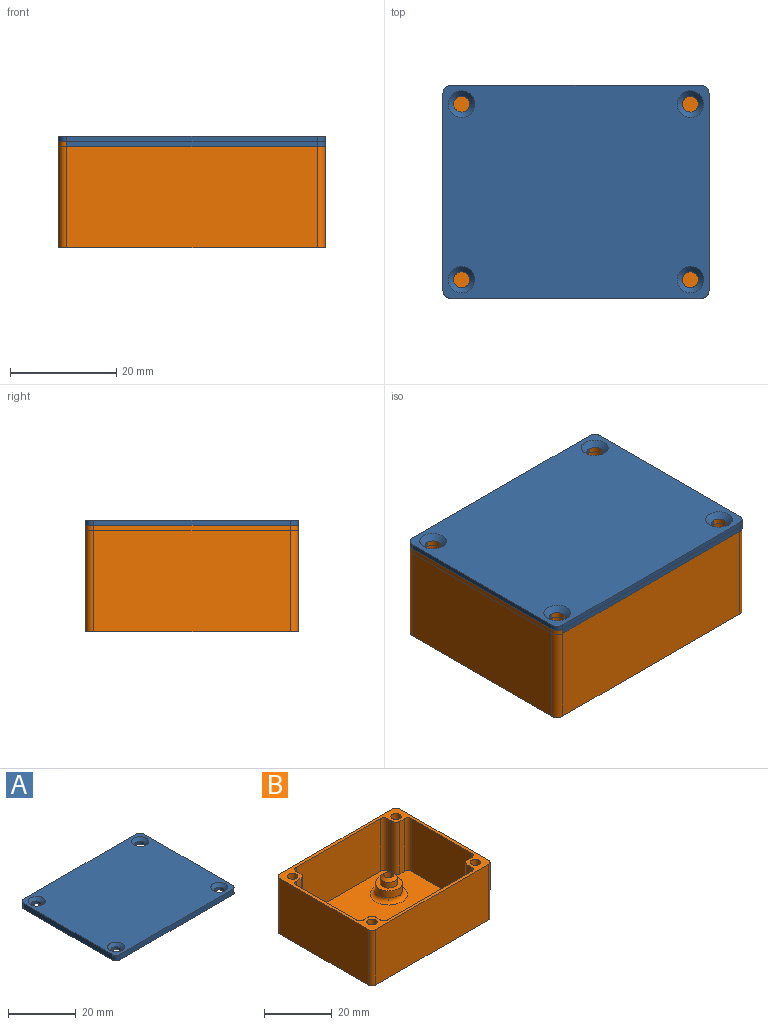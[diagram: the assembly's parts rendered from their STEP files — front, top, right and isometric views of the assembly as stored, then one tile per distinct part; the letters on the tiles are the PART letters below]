
ASSEMBLY  parts=2 mates=1
PART A: 18 faces, bbox 50x40x2 mm
  f0: plane 47x2mm, normal (0,1,0), area 94mm2, adj f4,f5,f14,f17
  f1: plane 37x2mm, normal (-1,0,0), area 74mm2, adj f4,f5,f14,f15
  f2: plane 47x2mm, normal (0,-1,0), area 94mm2, adj f4,f5,f15,f16
  f3: plane 37x2mm, normal (1,0,0), area 74mm2, adj f4,f5,f16,f17
  f4: plane 50x40mm, normal (0,0,1), area 1919.5mm2, adj f0,f1,f2,f3,f10,f11,f12,f13
  f5: plane 50x40mm, normal (0,0,-1), area 1969.8mm2, adj f0,f1,f2,f3,f6,f7,f8,f9
  f6: cylinder r=1.5mm len=3mm, axis (0,0,1), area 9.4mm2, adj f5,f13
  f7: cylinder r=1.5mm len=3mm, axis (0,0,1), area 9.4mm2, adj f5,f12
  f8: cylinder r=1.5mm len=3mm, axis (0,0,1), area 9.4mm2, adj f5,f11
  f9: cylinder r=1.5mm len=3mm, axis (0,0,1), area 9.4mm2, adj f5,f10
  f10: cone r=1.5mm half-angle=45deg, axis (0,0,1), area 17.8mm2, adj f4,f9
  f11: cone r=1.5mm half-angle=45deg, axis (0,0,1), area 17.8mm2, adj f4,f8
  f12: cone r=1.5mm half-angle=45deg, axis (0,0,1), area 17.8mm2, adj f4,f7
  f13: cone r=1.5mm half-angle=45deg, axis (0,0,1), area 17.8mm2, adj f4,f6
  f14: cylinder r=1.5mm len=2mm, axis (0,0,1), area 4.7mm2, adj f0,f1,f4,f5
  f15: cylinder r=1.5mm len=2mm, axis (0,0,-1), area 4.7mm2, adj f1,f2,f4,f5
  f16: cylinder r=1.5mm len=2mm, axis (0,0,1), area 4.7mm2, adj f2,f3,f4,f5
  f17: cylinder r=1.5mm len=2mm, axis (0,0,-1), area 4.7mm2, adj f0,f3,f4,f5
PART B: 95 faces, bbox 50x40x20 mm
  f0: cylinder r=1.5mm len=6mm, axis (0,0,-1), area 56.5mm2, adj f90,f94
  f1: cylinder r=1.5mm len=6mm, axis (0,0,-1), area 56.5mm2, adj f83,f91
  f2: cylinder r=1.5mm len=6mm, axis (0,0,-1), area 56.5mm2, adj f76,f93
  f3: cylinder r=1.5mm len=6mm, axis (0,0,-1), area 56.5mm2, adj f69,f92
  f4: plane 48x38mm, normal (0,0,1), area 1341.9mm2, adj f5,f6,f7,f8,f15,f16,f17,f18
  f5: plane 35x19mm, normal (0,1,0), area 665mm2, adj f4,f9,f48,f50
  f6: plane 25x19mm, normal (-1,0,0), area 475mm2, adj f4,f9,f52,f53
  f7: plane 35x19mm, normal (0,-1,0), area 665mm2, adj f4,f9,f54,f56
  f8: plane 25x19mm, normal (1,0,0), area 475mm2, adj f4,f9,f49,f58
  f9: plane 50x40mm, normal (0,0,1), area 247.7mm2, adj f5,f6,f7,f8,f10,f11,f12,f13
  f10: plane 47x20mm, normal (0,-1,0), area 940mm2, adj f9,f14,f59,f62
  f11: plane 37x20mm, normal (1,0,0), area 740mm2, adj f9,f14,f59,f60
  f12: plane 47x20mm, normal (0,1,0), area 940mm2, adj f9,f14,f60,f61
  f13: plane 37x20mm, normal (-1,0,0), area 740mm2, adj f9,f14,f61,f62
  f14: plane 50x40mm, normal (0,0,-1), area 1831.8mm2, adj f10,f11,f12,f13,f59,f60,f61,f62
  f15: plane 19x2mm, normal (0,-1,0), area 38mm2, adj f4,f9,f57,f58
  f16: plane 19x2mm, normal (1,0,0), area 38mm2, adj f4,f9,f56,f57
  f17: plane 19x2mm, normal (0,-1,0), area 38mm2, adj f4,f9,f53,f55
  f18: plane 19x2mm, normal (-1,0,0), area 38mm2, adj f4,f9,f54,f55
  f19: plane 19x2mm, normal (0,1,0), area 38mm2, adj f4,f9,f47,f49
  f20: plane 19x2mm, normal (1,0,0), area 38mm2, adj f4,f9,f47,f48
  f21: plane 19x2mm, normal (0,1,0), area 38mm2, adj f4,f9,f51,f52
  f22: plane 19x2mm, normal (-1,0,0), area 38mm2, adj f4,f9,f50,f51
  f23: cylinder r=1.5mm len=10mm, axis (0,0,1), area 94.2mm2, adj f9,f24
  f24: plane 3x3mm, normal (0,0,1), area 7.1mm2, adj f23
  f25: cylinder r=1.5mm len=10mm, axis (0,0,1), area 94.2mm2, adj f9,f26
  f26: plane 3x3mm, normal (0,0,1), area 7.1mm2, adj f25
  f27: cylinder r=1.5mm len=10mm, axis (0,0,1), area 94.2mm2, adj f9,f28
  f28: plane 3x3mm, normal (0,0,1), area 7.1mm2, adj f27
  f29: cylinder r=1.5mm len=10mm, axis (0,0,1), area 94.2mm2, adj f9,f30
  f30: plane 3x3mm, normal (0,0,1), area 7.1mm2, adj f29
  f31: cylinder r=2.5mm len=5mm, axis (0,0,-1), area 31.4mm2, adj f42,f94
  f32: cylinder r=2.5mm len=5mm, axis (0,0,-1), area 31.4mm2, adj f40,f91
  f33: cylinder r=2.5mm len=5mm, axis (0,0,-1), area 31.4mm2, adj f38,f93
  f34: cylinder r=2.5mm len=5mm, axis (0,0,-1), area 31.4mm2, adj f36,f92
  f35: cylinder r=4mm len=8mm, axis (0,0,-1), area 62.8mm2, adj f36,f46
  f36: plane 8x8mm, normal (0,0,1), area 30.6mm2, adj f34,f35
  f37: cylinder r=4mm len=8mm, axis (0,0,-1), area 62.8mm2, adj f38,f45
  f38: plane 8x8mm, normal (0,0,1), area 30.6mm2, adj f33,f37
  f39: cylinder r=4mm len=8mm, axis (0,0,-1), area 62.8mm2, adj f40,f44
  f40: plane 8x8mm, normal (0,0,1), area 30.6mm2, adj f32,f39
  f41: cylinder r=4mm len=8mm, axis (0,0,-1), area 62.8mm2, adj f42,f43
  f42: plane 8x8mm, normal (0,0,1), area 30.6mm2, adj f31,f41
  f43: torus R=5.5mm, axis (0,0,1), area 67.3mm2, adj f4,f41
  f44: torus R=5.5mm, axis (0,0,1), area 67.3mm2, adj f4,f39
  f45: torus R=5.5mm, axis (0,0,1), area 67.3mm2, adj f4,f37
  f46: torus R=5.5mm, axis (0,0,1), area 67.3mm2, adj f4,f35
  f47: cylinder r=1.5mm len=19mm, axis (0,0,1), area 44.8mm2, adj f4,f9,f19,f20
  f48: cylinder r=1.5mm len=19mm, axis (0,0,1), area 44.8mm2, adj f4,f5,f9,f20
  f49: cylinder r=1.5mm len=19mm, axis (0,0,-1), area 44.8mm2, adj f4,f8,f9,f19
  f50: cylinder r=1.5mm len=19mm, axis (0,0,-1), area 44.8mm2, adj f4,f5,f9,f22
  f51: cylinder r=1.5mm len=19mm, axis (0,0,1), area 44.8mm2, adj f4,f9,f21,f22
  f52: cylinder r=1.5mm len=19mm, axis (0,0,-1), area 44.8mm2, adj f4,f6,f9,f21
  f53: cylinder r=1.5mm len=19mm, axis (0,0,1), area 44.8mm2, adj f4,f6,f9,f17
  f54: cylinder r=1.5mm len=19mm, axis (0,0,-1), area 44.8mm2, adj f4,f7,f9,f18
  f55: cylinder r=1.5mm len=19mm, axis (0,0,1), area 44.8mm2, adj f4,f9,f17,f18
  f56: cylinder r=1.5mm len=19mm, axis (0,0,1), area 44.8mm2, adj f4,f7,f9,f16
  f57: cylinder r=1.5mm len=19mm, axis (0,0,1), area 44.8mm2, adj f4,f9,f15,f16
  f58: cylinder r=1.5mm len=19mm, axis (0,0,1), area 44.8mm2, adj f4,f8,f9,f15
  f59: cylinder r=1.5mm len=20mm, axis (0,0,1), area 47.1mm2, adj f9,f10,f11,f14
  f60: cylinder r=1.5mm len=20mm, axis (0,0,-1), area 47.1mm2, adj f9,f11,f12,f14
  f61: cylinder r=1.5mm len=20mm, axis (0,0,1), area 47.1mm2, adj f9,f12,f13,f14
  f62: cylinder r=1.5mm len=20mm, axis (0,0,-1), area 47.1mm2, adj f9,f10,f13,f14
  f63: plane 2.99x2.66mm, normal (0.66,-0.75,0), area 8mm2, adj f14,f64,f68,f69
  f64: plane 3.8x2mm, normal (-0.31,-0.95,0), area 8mm2, adj f14,f63,f65,f69
  f65: plane 3.92x2mm, normal (-0.98,-0.2,0), area 8mm2, adj f14,f64,f66,f69
  f66: plane 2.99x2.66mm, normal (-0.66,0.75,0), area 8mm2, adj f14,f65,f67,f69
  f67: plane 3.8x2mm, normal (0.31,0.95,0), area 8mm2, adj f14,f66,f68,f69
  f68: plane 3.92x2mm, normal (0.98,0.2,0), area 8mm2, adj f14,f63,f67,f69
  f69: plane 7.84x7.59mm, normal (0,0,-1), area 34.5mm2, adj f3,f63,f64,f65,f66,f67,f68
  f70: plane 2.89x2.76mm, normal (0.72,-0.69,0), area 8mm2, adj f14,f71,f75,f76
  f71: plane 3.89x2mm, normal (-0.24,-0.97,0), area 8mm2, adj f14,f70,f72,f76
  f72: plane 3.84x2mm, normal (-0.96,-0.28,0), area 8mm2, adj f14,f71,f73,f76
  f73: plane 2.89x2.76mm, normal (-0.72,0.69,0), area 8mm2, adj f14,f72,f74,f76
  f74: plane 3.89x2mm, normal (0.24,0.97,0), area 8mm2, adj f14,f73,f75,f76
  f75: plane 3.84x2mm, normal (0.96,0.28,0), area 8mm2, adj f14,f70,f74,f76
  f76: plane 7.77x7.68mm, normal (0,0,-1), area 34.5mm2, adj f2,f70,f71,f72,f73,f74,f75
  f77: plane 2.92x2.73mm, normal (-0.68,0.73,0), area 8mm2, adj f14,f78,f82,f83
  f78: plane 3.83x2mm, normal (0.29,0.96,0), area 8mm2, adj f14,f77,f79,f83
  f79: plane 3.9x2mm, normal (0.97,0.23,0), area 8mm2, adj f14,f78,f80,f83
  f80: plane 2.92x2.73mm, normal (0.68,-0.73,0), area 8mm2, adj f14,f79,f81,f83
  f81: plane 3.83x2mm, normal (-0.29,-0.96,0), area 8mm2, adj f14,f80,f82,f83
  f82: plane 3.9x2mm, normal (-0.97,-0.23,0), area 8mm2, adj f14,f77,f81,f83
  f83: plane 7.79x7.65mm, normal (0,0,-1), area 34.5mm2, adj f1,f77,f78,f79,f80,f81,f82
  f84: plane 3.88x2mm, normal (-0.97,-0.24,0), area 8mm2, adj f14,f85,f89,f90
  f85: plane 2.88x2.78mm, normal (-0.69,0.72,0), area 8mm2, adj f14,f84,f86,f90
  f86: plane 3.84x2mm, normal (0.28,0.96,0), area 8mm2, adj f14,f85,f87,f90
  f87: plane 3.88x2mm, normal (0.97,0.24,0), area 8mm2, adj f14,f86,f88,f90
  f88: plane 2.88x2.78mm, normal (0.69,-0.72,0), area 8mm2, adj f14,f87,f89,f90
  f89: plane 3.84x2mm, normal (-0.28,-0.96,0), area 8mm2, adj f14,f84,f88,f90
  f90: plane 7.76x7.69mm, normal (0,0,-1), area 34.5mm2, adj f0,f84,f85,f86,f87,f88,f89
  f91: cone r=1.5mm half-angle=45deg, axis (0,0,-1), area 17.8mm2, adj f1,f32
  f92: cone r=1.5mm half-angle=45deg, axis (0,0,-1), area 17.8mm2, adj f3,f34
  f93: cone r=1.5mm half-angle=45deg, axis (0,0,-1), area 17.8mm2, adj f2,f33
  f94: cone r=1.5mm half-angle=45deg, axis (0,0,-1), area 17.8mm2, adj f0,f31
PLACE A t=(53.47,-82,19)mm
PLACE B at identity fixed
MATE slider B.f29 <-> A.f6  axis (0,0,1) through (8.02,-24.46,20)mm
